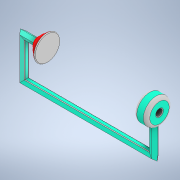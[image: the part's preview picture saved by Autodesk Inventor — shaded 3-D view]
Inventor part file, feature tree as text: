
AUTODESK INVENTOR PART (.ipt)
format: ipt  version: 2021 (Build 250183000, 183)  size: 275,968 bytes
history: native  units: mm
features: sketch x5, fillet x3, plane x2, extrude x2, sweep x1, revolve x1, thread x1
ambient origin geometry x8: Origin, YZ Plane, XZ Plane, XY Plane, X Axis, Y Axis, Z Axis, Center Point
bodies: Solid1 (feature_tree)
feature tree (15):
  sketch  "Sketch1"  dims[d0=60.0mm d1=200.0mm]
  plane  "Work Plane1"
  sweep  "Sweep1"
  revolve  "Revolution1"  [1 undecoded]
  fillet  "Fillet1"  Radius=100.0mm
  plane  "Work Plane2"
  extrude  "Extrusion1"  Depth=10.0mm
  extrude  "Extrusion2"  Depth=10.0mm
  thread  "Thread1"  [1 undecoded]
  fillet  "Fillet2"  Radius=10.0mm
  fillet  "Fillet3"  Radius=5.0mm
  sketch  "Sketch2"  dims[d2=45.0mm d3=20.0mm d4=100.0mm]
  sketch  "Sketch3"  dims[d5=0.0mm d6=10.0mm]
  sketch  "Sketch4"  dims[d7=0.0mm d8=0.0mm d9=20.0mm d10=15.0mm d11=10.0mm d12=5.0mm]
  sketch  "Sketch5"  dims[d13=6.0mm d14=5.0mm d15=5.0mm d16=90.0deg d17=5.0mm d18=20.0mm d19=0.0mm d20=10.0mm d21=20.0mm d22=0.0mm d23=130.0mm d24=0.0mm d25=5.0mm d26=1.0mm]
note: 2 required parameter values undecoded (feature->parameter linkage not recoverable at this tier; creation-order binding heuristic only, values carry confidence <= 0.55)